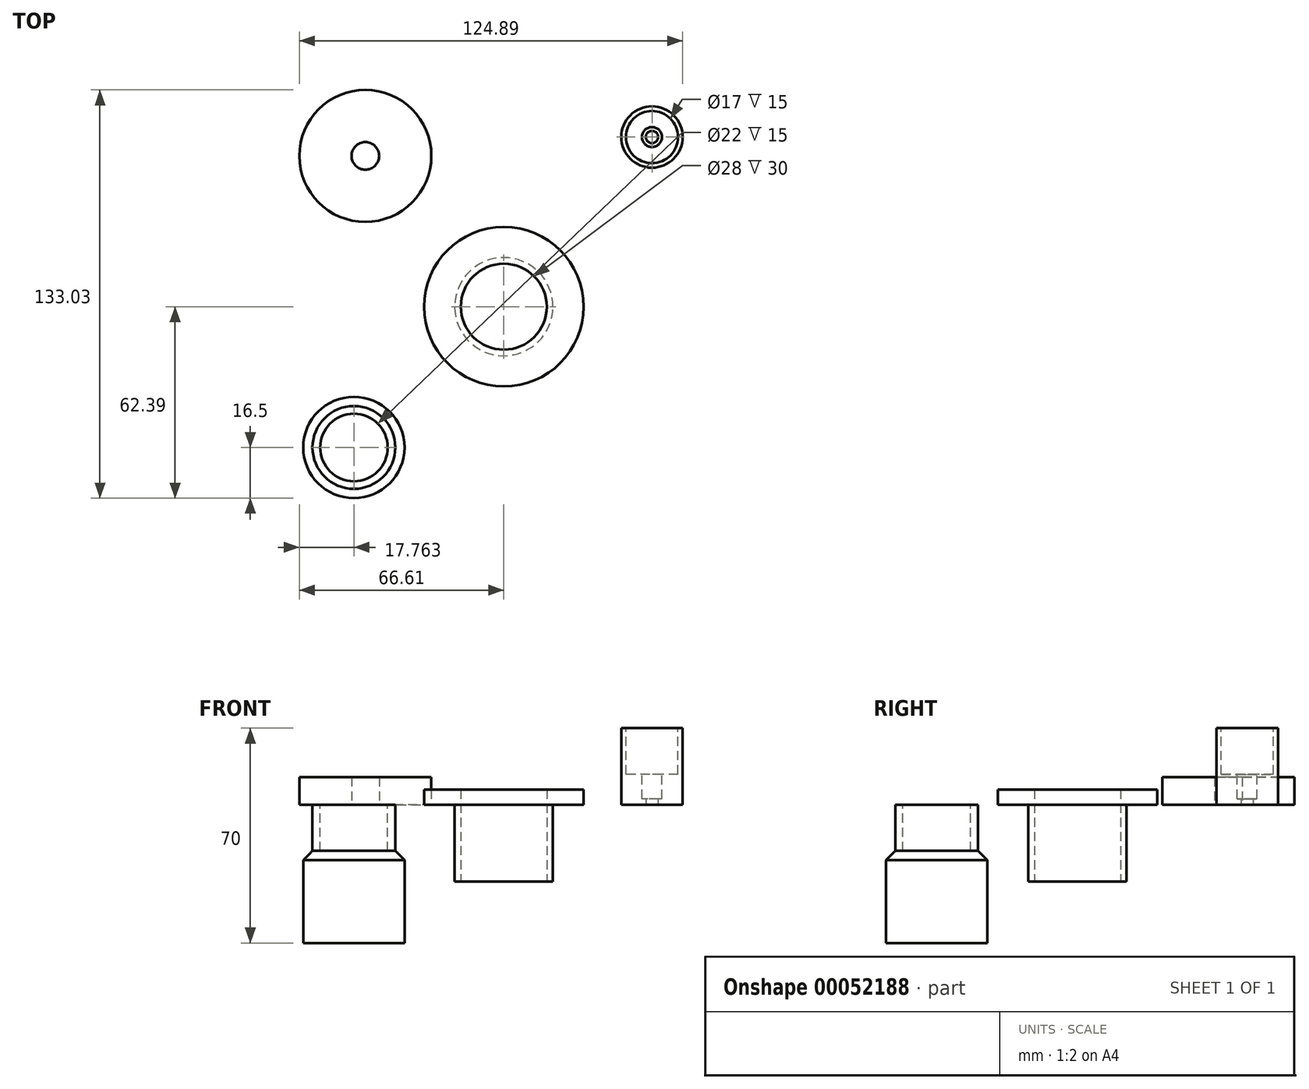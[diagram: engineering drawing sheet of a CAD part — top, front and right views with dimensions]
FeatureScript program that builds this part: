
annotation { "Feature Type Name" : "Feature", "Feature Type Description" : "" }
export const myFeature = defineFeature(function(context is Context, id is Id, definition is map)
    precondition{}
    {
        {
            var Q0;
            Q0=qCreatedBy(makeId("Top.planeOp"),FACE);
            var sketch = newSketch(context, id + "F0", { "sketchPlane" : qUnion([Q0])});
            skCircle(sketch, "E0", {"center": v(0, 0) * mm, "radius": 26 * mm});
            skCircle(sketch, "E1", {"center": v(0, 0) * mm, "radius": 14 * mm});
            skSolve(sketch);
        }
        {
            var Q0;
            Q0 = qSketchRegion(id + "F0", true);
            extrude(context, id + "F1", {"entities" : qUnion([Q0]), "depth" : 5 * mm});
        }
        {
            var Q0;
            Q0=makeQuery(id+"F1.opExtrude","CAP_FACE",FACE,{"disambiguationData":[OSD([sQuery(id+"F0.wireOp",EDGE,"E0"),sQuery(id+"F0.wireOp",EDGE,"E1")])],"isStart":true});
            var sketch = newSketch(context, id + "F2", { "sketchPlane" : qUnion([Q0])});
            skCircle(sketch, "E2", {"center": v(0, 0) * mm, "radius": 16 * mm});
            skCircle(sketch, "E3", {"center": v(0, 0) * mm, "radius": 14 * mm});
            skSolve(sketch);
        }
        {
            var Q0;
            Q0 = qSketchRegion(id + "F2", true);
            extrude(context, id + "F3", {"entities" : qUnion([Q0]), "operationType" : NewBodyOperationType.ADD, "depth" : 25 * mm});
        }
        {
            var Q0;
            Q0=qCreatedBy(makeId("Top.planeOp"),FACE);
            var sketch = newSketch(context, id + "F4", { "sketchPlane" : qUnion([Q0])});
            skCircle(sketch, "E4", {"center": v(-48.85, -45.89) * mm, "radius": 13.5 * mm});
            skCircle(sketch, "E5", {"center": v(-48.85, -45.89) * mm, "radius": 11 * mm});
            skSolve(sketch);
        }
        {
            var Q0;
            Q0 = qSketchRegion(id + "F4", true);
            extrude(context, id + "F5", {"entities" : qUnion([Q0]), "oppositeDirection" : true, "depth" : 15 * mm});
        }
        {
            var Q0;
            Q0=makeQuery(id+"F5.opExtrude","CAP_FACE",FACE,{"disambiguationData":[OSD([sQuery(id+"F4.wireOp",EDGE,"E4"),sQuery(id+"F4.wireOp",EDGE,"E5")])],"isStart":false});
            var sketch = newSketch(context, id + "F6", { "sketchPlane" : qUnion([Q0])});
            skCircle(sketch, "E6", {"center": v(-48.85, 45.89) * mm, "radius": 16.5 * mm});
            skSolve(sketch);
        }
        {
            var Q0;
            Q0 = qSketchRegion(id + "F6", true);
            extrude(context, id + "F7", {"entities" : qUnion([Q0]), "operationType" : NewBodyOperationType.ADD, "depth" : 30 * mm});
        }
        {
            var Q0;
            Q0=makeQuery(id+"F7.opExtrude","CAP_EDGE",EDGE,{"disambiguationData":[OSD([sQuery(id+"F6.wireOp",EDGE,"E6")])],"isStart":true});
            chamfer(context, id + "F8", {"entities" : qUnion([Q0]), "chamferType" : ChamferType.OFFSET_ANGLE, "width" : 3 * mm, "oppositeDirection" : false, "angle" : 45 * degree, "tangentPropagation" : true});
        }
        {
            var Q0;
            Q0=qCreatedBy(makeId("Top.planeOp"),FACE);
            var sketch = newSketch(context, id + "F9", { "sketchPlane" : qUnion([Q0])});
            skCircle(sketch, "E7", {"center": v(48.28, 55.3) * mm, "radius": 2 * mm});
            skCircle(sketch, "E8", {"center": v(48.28, 55.3) * mm, "radius": 10 * mm});
            skSolve(sketch);
        }
        {
            var Q0;
            Q0 = qSketchRegion(id + "F9", true);
            extrude(context, id + "F10", {"entities" : qUnion([Q0]), "depth" : 25 * mm});
        }
        {
            var Q0;
            Q0=makeQuery(id+"F10.opExtrude","CAP_FACE",FACE,{"disambiguationData":[OSD([sQuery(id+"F9.wireOp",EDGE,"E7"),sQuery(id+"F9.wireOp",EDGE,"E8")])],"isStart":false});
            var sketch = newSketch(context, id + "F11", { "sketchPlane" : qUnion([Q0])});
            skCircle(sketch, "E9", {"center": v(48.28, 55.3) * mm, "radius": 8.5 * mm});
            skSolve(sketch);
        }
        {
            var Q0;
            Q0 = qSketchRegion(id + "F11", true);
            extrude(context, id + "F12", {"entities" : qUnion([Q0]), "operationType" : NewBodyOperationType.REMOVE, "oppositeDirection" : true, "depth" : 15 * mm});
        }
        {
            var Q0;
            Q0=makeQuery(id+"F12.boolean.opBoolean","COPY",FACE,{"derivedFrom":makeQuery(id+"F12.opExtrude","CAP_FACE",FACE,{"disambiguationData":[OSD([sQuery(id+"F11.wireOp",EDGE,"E9")])],"isStart":false})});
            var sketch = newSketch(context, id + "F13", { "sketchPlane" : qUnion([Q0])});
            skCircle(sketch, "E10", {"center": v(48.28, 55.3) * mm, "radius": 3.25 * mm});
            skSolve(sketch);
        }
        {
            var Q0;
            Q0 = qSketchRegion(id + "F13", true);
            extrude(context, id + "F14", {"entities" : qUnion([Q0]), "operationType" : NewBodyOperationType.REMOVE, "oppositeDirection" : true, "depth" : 8 * mm});
        }
        {
            var Q0;
            Q0=qCreatedBy(makeId("Top.planeOp"),FACE);
            var sketch = newSketch(context, id + "F15", { "sketchPlane" : qUnion([Q0])});
            skCircle(sketch, "E11", {"center": v(-45.11, 49.14) * mm, "radius": 21.5 * mm});
            skCircle(sketch, "E12", {"center": v(-45.11, 49.14) * mm, "radius": 4.5 * mm});
            skSolve(sketch);
        }
        {
            var Q0;
            Q0 = qSketchRegion(id + "F15", true);
            extrude(context, id + "F16", {"entities" : qUnion([Q0]), "depth" : 9 * mm});
        }
    });
